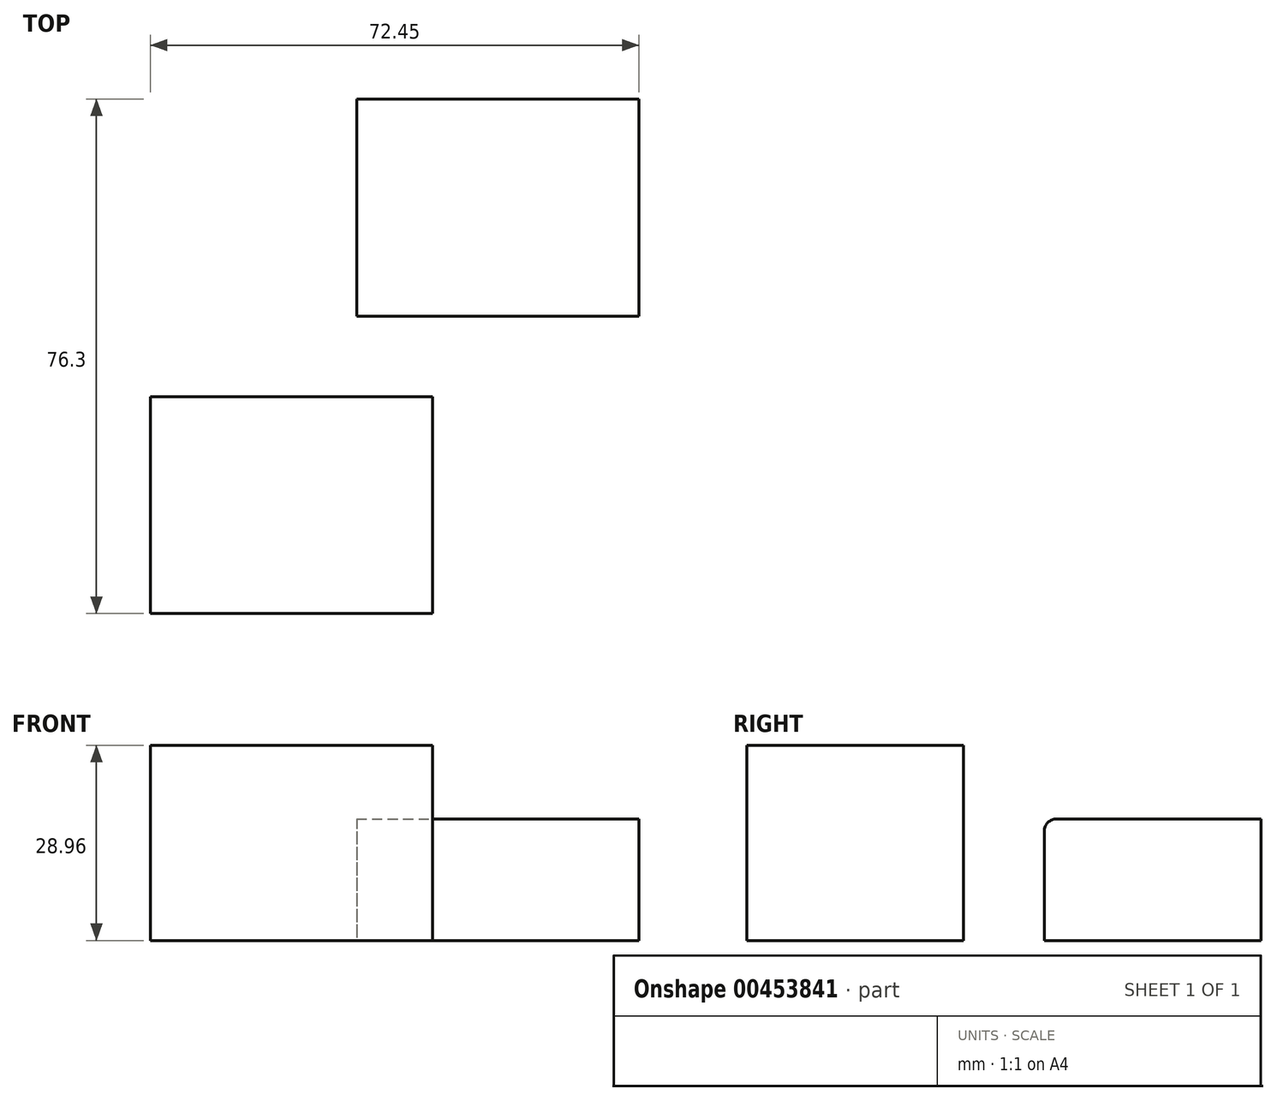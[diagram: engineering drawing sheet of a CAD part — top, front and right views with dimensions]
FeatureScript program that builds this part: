
annotation { "Feature Type Name" : "Feature", "Feature Type Description" : "" }
export const myFeature = defineFeature(function(context is Context, id is Id, definition is map)
    precondition{}
    {
        {
            var Q0;
            Q0=qCreatedBy(makeId("Top.planeOp"),FACE);
            var sketch = newSketch(context, id + "F0", { "sketchPlane" : qUnion([Q0])});
            skLineSegment(sketch, "E0.bottom", {"start": v(-17.12, 14.23) * mm, "end": v(24.75, 14.23) * mm});
            skLineSegment(sketch, "E0.top", {"start": v(-17.12, -17.94) * mm, "end": v(24.75, -17.94) * mm});
            skLineSegment(sketch, "E0.left", {"start": v(-17.12, 14.23) * mm, "end": v(-17.12, -17.94) * mm});
            skLineSegment(sketch, "E0.right", {"start": v(24.75, 14.23) * mm, "end": v(24.75, -17.94) * mm});
            skLineSegment(sketch, "E1.bottom", {"start": v(13.47, 58.36) * mm, "end": v(55.33, 58.36) * mm});
            skLineSegment(sketch, "E1.top", {"start": v(13.47, 26.19) * mm, "end": v(55.33, 26.19) * mm});
            skLineSegment(sketch, "E1.left", {"start": v(13.47, 58.36) * mm, "end": v(13.47, 26.19) * mm});
            skLineSegment(sketch, "E1.right", {"start": v(55.33, 58.36) * mm, "end": v(55.33, 26.19) * mm});
            skSolve(sketch);
        }
        {
            var Q0;
            Q0=makeQuery(id+"F0.imprint","IMPRINT",FACE,{"disambiguationData":[TD([[makeQuery(id+"F0.imprint","IMPRINT",EDGE,{"derivedFrom":sQuery(id+"F0.wireOp",EDGE,"E1.bottom")}),-1.0]])]});
            extrude(context, id + "F1", {"entities" : qUnion([Q0]), "depth" : 18.03 * mm});
        }
        {
            var Q0;
            Q0=makeQuery(id+"F1.opExtrude","CAP_EDGE",EDGE,{"disambiguationData":[OSD([sQuery(id+"F0.wireOp",EDGE,"E1.top")])],"isStart":false});
            fillet(context, id + "F2", {"entities" : qUnion([Q0]), "radius" : 1.84 * mm, "tangentPropagation" : true, "allowEdgeOverflow" : false});
        }
        {
            var Q0;
            Q0=makeQuery(id+"F0.imprint","IMPRINT",FACE,{"disambiguationData":[TD([[makeQuery(id+"F0.imprint","IMPRINT",EDGE,{"derivedFrom":sQuery(id+"F0.wireOp",EDGE,"E0.bottom")}),-1.0]])]});
            extrude(context, id + "F3", {"entities" : qUnion([Q0]), "depth" : 28.96 * mm});
        }
    });
